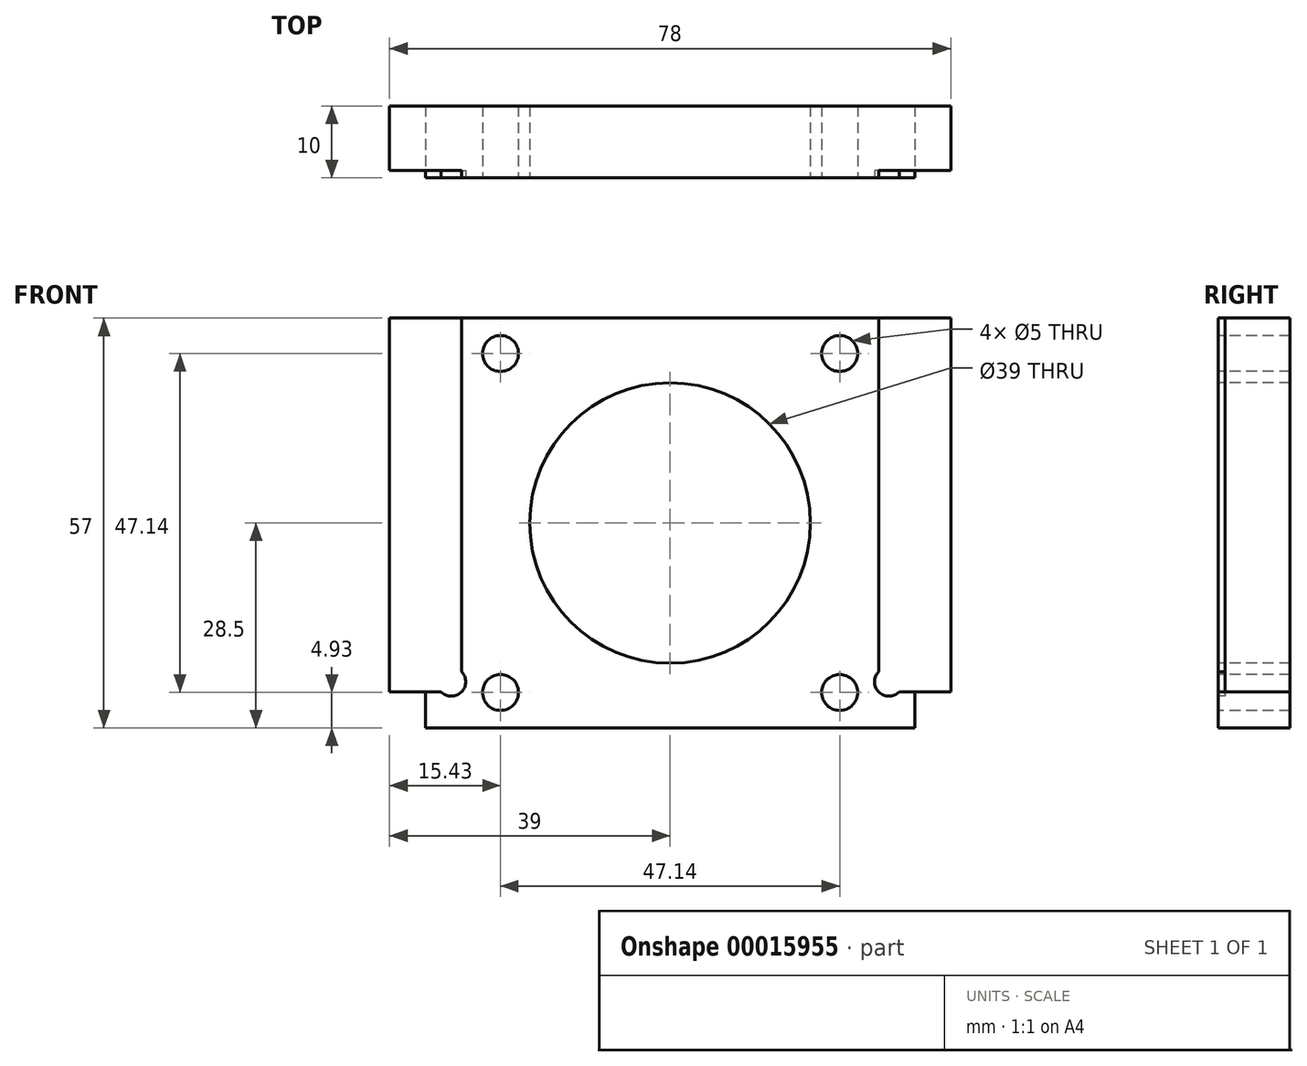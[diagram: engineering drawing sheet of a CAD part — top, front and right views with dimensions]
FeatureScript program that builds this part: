
annotation { "Feature Type Name" : "Feature", "Feature Type Description" : "" }
export const myFeature = defineFeature(function(context is Context, id is Id, definition is map)
    precondition{}
    {
        {
            var Q0;
            Q0=qCreatedBy(makeId("Front.planeOp"),FACE);
            var sketch = newSketch(context, id + "F0", { "sketchPlane" : qUnion([Q0])});
            skLineSegment(sketch, "E0.bottom", {"start": v(5, 0) * mm, "end": v(73, 0) * mm});
            skLineSegment(sketch, "E0.top", {"start": v(0, 57) * mm, "end": v(78, 57) * mm});
            skLineSegment(sketch, "E0.left", {"start": v(0, 4.93) * mm, "end": v(0, 57) * mm});
            skLineSegment(sketch, "E0.right", {"start": v(78, 4.93) * mm, "end": v(78, 57) * mm});
            skLineSegment(sketch, "E1", {"start": v(0, 57) * mm, "end": v(78, 0) * mm, "construction": true});
            skLineSegment(sketch, "E2", {"start": v(78, 57) * mm, "end": v(0, 0) * mm, "construction": true});
            skCircle(sketch, "E3", {"center": v(39, 28.5) * mm, "radius": 19.5 * mm});
            skLineSegment(sketch, "E4", {"start": v(39, 57) * mm, "end": v(39, 0) * mm, "construction": true});
            skLineSegment(sketch, "E5", {"start": v(0, 28.5) * mm, "end": v(78, 28.5) * mm, "construction": true});
            skLineSegment(sketch, "E6.0", {"start": v(15.43, 57) * mm, "end": v(15.43, 0) * mm, "construction": true});
            skLineSegment(sketch, "E7.0", {"start": v(0, 4.93) * mm, "end": v(78, 4.93) * mm, "construction": true});
            skCircle(sketch, "E8", {"center": v(15.43, 4.93) * mm, "radius": 2.5 * mm});
            skCircle(sketch, "E9.MirrorC", {"center": v(15.43, 52.07) * mm, "radius": 2.5 * mm});
            skCircle(sketch, "E10.MirrorC", {"center": v(62.57, 52.07) * mm, "radius": 2.5 * mm});
            skCircle(sketch, "E11.MirrorC", {"center": v(62.57, 4.93) * mm, "radius": 2.5 * mm});
            skLineSegment(sketch, "E12.top", {"start": v(0, 5) * mm, "end": v(5, 5) * mm});
            skLineSegment(sketch, "E12.left", {"start": v(0, 4.93) * mm, "end": v(0, 5) * mm});
            skLineSegment(sketch, "E12.right", {"start": v(5, 0) * mm, "end": v(5, 5) * mm});
            skLineSegment(sketch, "E13.top", {"start": v(78, 5) * mm, "end": v(73, 5) * mm});
            skLineSegment(sketch, "E13.left", {"start": v(78, 4.93) * mm, "end": v(78, 5) * mm});
            skLineSegment(sketch, "E13.right", {"start": v(73, 0) * mm, "end": v(73, 5) * mm});
            skSolve(sketch);
        }
        {
            var Q0;
            Q0 = qSketchRegion(id + "F0", true);
            extrude(context, id + "F1", {"entities" : qUnion([Q0]), "oppositeDirection" : true, "depth" : 10 * mm});
        }
        {
            var Q0;
            Q0=makeQuery(id+"F1.opExtrude","CAP_FACE",FACE,{"disambiguationData":[OSD([sQuery(id+"F0.wireOp",EDGE,"E0.bottom"),sQuery(id+"F0.wireOp",EDGE,"E0.top"),sQuery(id+"F0.wireOp",EDGE,"E0.left"),sQuery(id+"F0.wireOp",EDGE,"E0.right"),sQuery(id+"F0.wireOp",EDGE,"E3"),sQuery(id+"F0.wireOp",EDGE,"E8"),sQuery(id+"F0.wireOp",EDGE,"E9.MirrorC"),sQuery(id+"F0.wireOp",EDGE,"E10.MirrorC"),sQuery(id+"F0.wireOp",EDGE,"E11.MirrorC"),sQuery(id+"F0.wireOp",EDGE,"E12.top"),sQuery(id+"F0.wireOp",EDGE,"E12.right"),sQuery(id+"F0.wireOp",EDGE,"E13.top"),sQuery(id+"F0.wireOp",EDGE,"E13.right")])],"isStart":true});
            var sketch = newSketch(context, id + "F2", { "sketchPlane" : qUnion([Q0])});
            skLineSegment(sketch, "E14", {"start": v(39, 28.5) * mm, "end": v(39, 57) * mm, "construction": true});
            skLineSegment(sketch, "E15.0", {"start": v(10, 5) * mm, "end": v(10, 57) * mm, "construction": true});
            skPoint(sketch, "E16.rect.middle", {"position": v(39, 28.5) * mm});
            skLineSegment(sketch, "E17.bottom", {"start": v(0, 5) * mm, "end": v(10, 5) * mm});
            skLineSegment(sketch, "E17.top", {"start": v(0, 57) * mm, "end": v(10, 57) * mm});
            skLineSegment(sketch, "E17.left", {"start": v(0, 5) * mm, "end": v(0, 57) * mm});
            skLineSegment(sketch, "E17.right", {"start": v(10, 5) * mm, "end": v(10, 57) * mm});
            skLineSegment(sketch, "E18.MirrorCS", {"start": v(68, 5) * mm, "end": v(68, 57) * mm});
            skLineSegment(sketch, "E19.MirrorCS", {"start": v(78, 57) * mm, "end": v(68, 57) * mm});
            skLineSegment(sketch, "E20.MirrorCS", {"start": v(78, 5) * mm, "end": v(78, 57) * mm});
            skLineSegment(sketch, "E21.MirrorCS", {"start": v(78, 5) * mm, "end": v(68, 5) * mm});
            skSolve(sketch);
        }
        {
            var Q0;
            Q0 = qSketchRegion(id + "F2", true);
            extrude(context, id + "F3", {"entities" : qUnion([Q0]), "operationType" : NewBodyOperationType.REMOVE, "oppositeDirection" : true, "depth" : 1 * mm});
        }
        {
            var Q0;
            Q0=makeQuery(id+"F1.opExtrude","CAP_FACE",FACE,{"disambiguationData":[OSD([sQuery(id+"F0.wireOp",EDGE,"E0.bottom"),sQuery(id+"F0.wireOp",EDGE,"E0.top"),sQuery(id+"F0.wireOp",EDGE,"E0.left"),sQuery(id+"F0.wireOp",EDGE,"E0.right"),sQuery(id+"F0.wireOp",EDGE,"E3"),sQuery(id+"F0.wireOp",EDGE,"E8"),sQuery(id+"F0.wireOp",EDGE,"E9.MirrorC"),sQuery(id+"F0.wireOp",EDGE,"E10.MirrorC"),sQuery(id+"F0.wireOp",EDGE,"E11.MirrorC"),sQuery(id+"F0.wireOp",EDGE,"E12.top"),sQuery(id+"F0.wireOp",EDGE,"E12.right"),sQuery(id+"F0.wireOp",EDGE,"E13.top"),sQuery(id+"F0.wireOp",EDGE,"E13.right")])],"isStart":true});
            var sketch = newSketch(context, id + "F4", { "sketchPlane" : qUnion([Q0])});
            skLineSegment(sketch, "E22", {"start": v(39, 28.5) * mm, "end": v(39, 57) * mm, "construction": true});
            skCircle(sketch, "E23.MirrorC", {"center": v(8.59, 6.41) * mm, "radius": 2 * mm});
            skCircle(sketch, "E24.MirrorC", {"center": v(69.41, 6.41) * mm, "radius": 2 * mm});
            skSolve(sketch);
        }
        {
            var Q0;
            Q0 = qSketchRegion(id + "F4", true);
            extrude(context, id + "F5", {"entities" : qUnion([Q0]), "operationType" : NewBodyOperationType.REMOVE, "oppositeDirection" : true, "depth" : 1 * mm});
        }
    });
